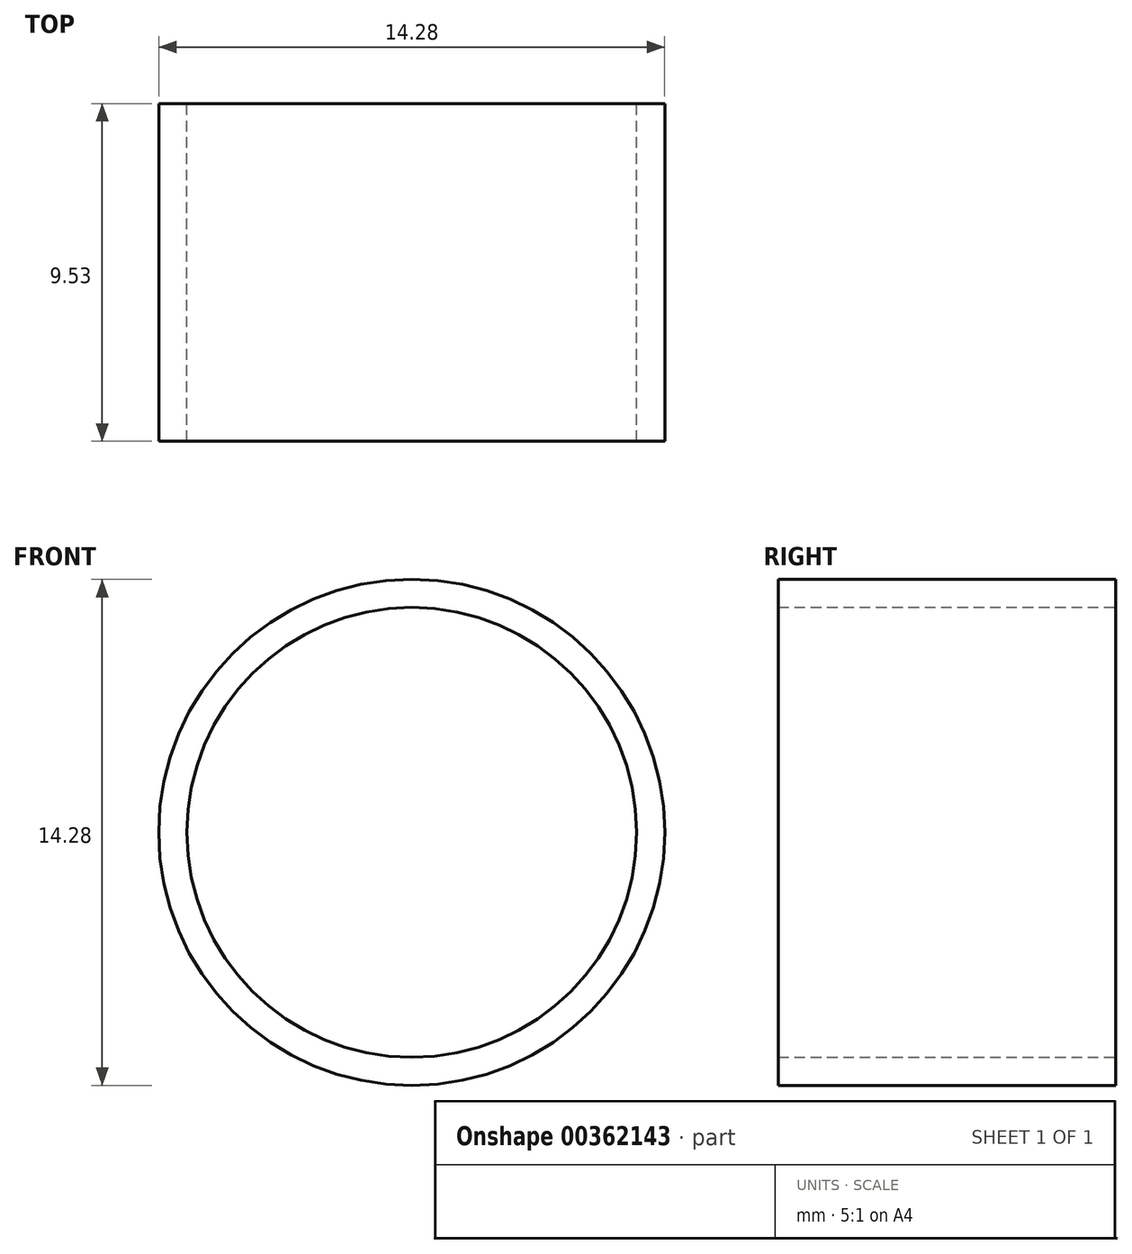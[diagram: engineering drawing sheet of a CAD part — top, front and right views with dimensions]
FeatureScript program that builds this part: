
annotation { "Feature Type Name" : "Feature", "Feature Type Description" : "" }
export const myFeature = defineFeature(function(context is Context, id is Id, definition is map)
    precondition{}
    {
        {
            var Q0;
            Q0=qCreatedBy(makeId("Front.planeOp"),FACE);
            var sketch = newSketch(context, id + "F0", { "sketchPlane" : qUnion([Q0])});
            skCircle(sketch, "E0", {"center": v(0, 0) * mm, "radius": 6.35 * mm});
            skCircle(sketch, "E1", {"center": v(0, 0) * mm, "radius": 7.14 * mm});
            skSolve(sketch);
        }
        {
            var Q0;
            Q0=makeQuery(id+"F0.imprint","IMPRINT",FACE,{"disambiguationData":[TD([[makeQuery(id+"F0.imprint","IMPRINT",EDGE,{"derivedFrom":sQuery(id+"F0.wireOp",EDGE,"E0")}),-1.0]])]});
            extrude(context, id + "F1", {"entities" : qUnion([Q0]), "depth" : 9.52 * mm, "offsetDistance" : 25.4 * mm});
        }
    });
